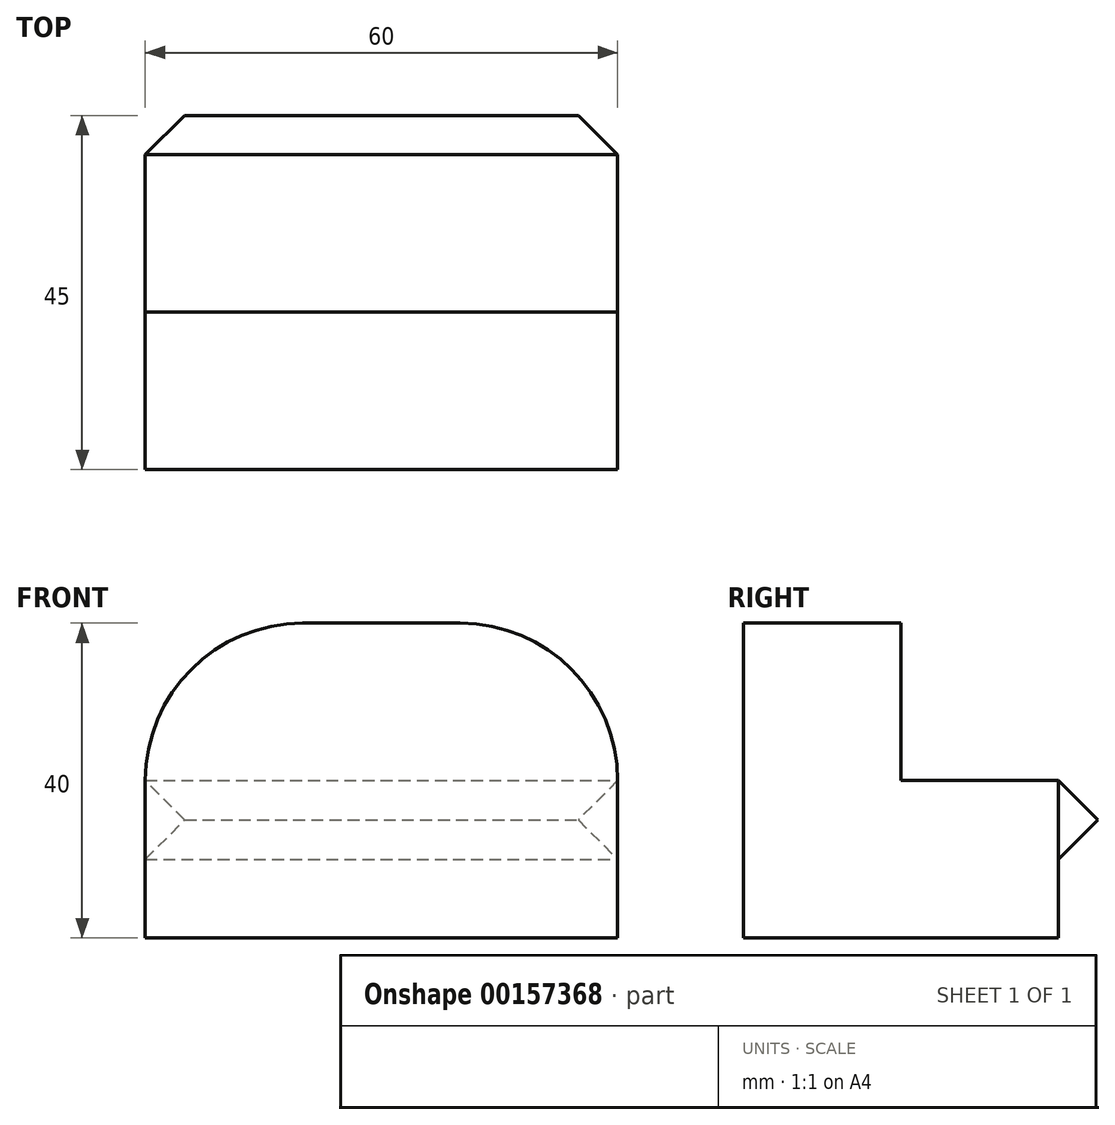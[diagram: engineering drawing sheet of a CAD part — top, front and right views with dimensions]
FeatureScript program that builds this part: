
annotation { "Feature Type Name" : "Feature", "Feature Type Description" : "" }
export const myFeature = defineFeature(function(context is Context, id is Id, definition is map)
    precondition{}
    {
        {
            var Q0;
            Q0=qCreatedBy(makeId("Top.planeOp"),FACE);
            var sketch = newSketch(context, id + "F0", { "sketchPlane" : qUnion([Q0])});
            skLineSegment(sketch, "E0.bottom", {"start": v(0, 0) * mm, "end": v(-60, 0) * mm});
            skLineSegment(sketch, "E0.top", {"start": v(0, 40) * mm, "end": v(-60, 40) * mm});
            skLineSegment(sketch, "E0.left", {"start": v(0, 0) * mm, "end": v(0, 40) * mm});
            skLineSegment(sketch, "E0.right", {"start": v(-60, 0) * mm, "end": v(-60, 40) * mm});
            skLineSegment(sketch, "E1", {"start": v(-60, 20) * mm, "end": v(0, 20) * mm});
            skLineSegment(sketch, "E2", {"start": v(-60, 20) * mm, "end": v(-30, 0) * mm});
            skSolve(sketch);
        }
        {
            var Q0;
            {var subQ4=sQuery(id+"F0.wireOp",EDGE,"E1");Q0=makeQuery(id+"F0.imprint","IMPRINT",FACE,{"disambiguationData":[TD([[makeQuery(id+"F0.imprint","IMPRINT",EDGE,{"derivedFrom":subQ4}),-1.0]])]});}
            extrude(context, id + "F1", {"entities" : qUnion([Q0]), "depth" : 40 * mm});
        }
        {
            var Q0;
            {var subQ3=sQuery(id+"F0.wireOp",EDGE,"E2");Q0=makeQuery(id+"F0.imprint","IMPRINT",FACE,{"disambiguationData":[TD([[makeQuery(id+"F0.imprint","IMPRINT",EDGE,{"derivedFrom":subQ3}),-1.0]])]});}
            extrude(context, id + "F2", {"entities" : qUnion([Q0]), "operationType" : NewBodyOperationType.ADD, "depth" : 40 * mm});
        }
        {
            var Q0;
            {var subQ0=sQuery(id+"F0.wireOp",EDGE,"E0.top");Q0=makeQuery(id+"F0.imprint","IMPRINT",FACE,{"disambiguationData":[TD([[makeQuery(id+"F0.imprint","IMPRINT",EDGE,{"derivedFrom":subQ0}),1.0]])]});}
            extrude(context, id + "F3", {"entities" : qUnion([Q0]), "operationType" : NewBodyOperationType.ADD, "depth" : 20 * mm});
        }
        {
            var Q0;
            Q0=makeQuery(id+"F3.opExtrude","CAP_FACE",FACE,{"disambiguationData":[OSD([sQuery(id+"F0.wireOp",EDGE,"E0.top"),sQuery(id+"F0.wireOp",EDGE,"E0.left"),sQuery(id+"F0.wireOp",EDGE,"E0.right"),sQuery(id+"F0.wireOp",EDGE,"E1")])],"isStart":false});
            var sketch = newSketch(context, id + "F4", { "sketchPlane" : qUnion([Q0])});
            skLineSegment(sketch, "E3", {"start": v(0, 20) * mm, "end": v(-19.98, 40) * mm});
            skSolve(sketch);
        }
        {
            var Q0;
            Q0=makeQuery(id+"F3.opExtrude","SWEPT_FACE",FACE,{"disambiguationData":[OSD([sQuery(id+"F0.wireOp",EDGE,"E0.top")])]});
            var sketch = newSketch(context, id + "F5", { "sketchPlane" : qUnion([Q0])});
            skLineSegment(sketch, "E4", {"start": v(0, 10) * mm, "end": v(60, 10) * mm});
            skSolve(sketch);
        }
        {
            var Q0;
            Q0 = qSketchRegion(id + "F5", true);
            var Q1;
            {var subQ0=sQuery(id+"F5.wireOp",EDGE,"E4");Q1=makeQuery(id+"F5.imprint","IMPRINT",FACE,{"disambiguationData":[TD([[makeQuery(id+"F5.imprint","IMPRINT",EDGE,{"derivedFrom":subQ0}),1.0]])]});}
            extrude(context, id + "F6", {"entities" : qUnion([Q0, Q1]), "operationType" : NewBodyOperationType.ADD, "depth" : 5.58 * mm, "hasDraft" : true, "draftAngle" : 45 * degree, "draftPullDirection" : true});
        }
        {
            var Q0;
            Q0=makeQuery(id+"F1.opExtrude","CAP_EDGE",EDGE,{"disambiguationData":[OSD([sQuery(id+"F0.wireOp",EDGE,"E0.left")])],"isStart":false});
            fillet(context, id + "F7", {"entities" : qUnion([Q0]), "radius" : 20 * mm, "tangentPropagation" : true, "allowEdgeOverflow" : false});
        }
        {
            var Q0;
            Q0=makeQuery(id+"F2.opExtrude","CAP_EDGE",EDGE,{"disambiguationData":[OSD([sQuery(id+"F0.wireOp",EDGE,"E0.right")])],"isStart":false});
            fillet(context, id + "F8", {"entities" : qUnion([Q0]), "radius" : 20 * mm, "tangentPropagation" : true, "allowEdgeOverflow" : false});
        }
    });
